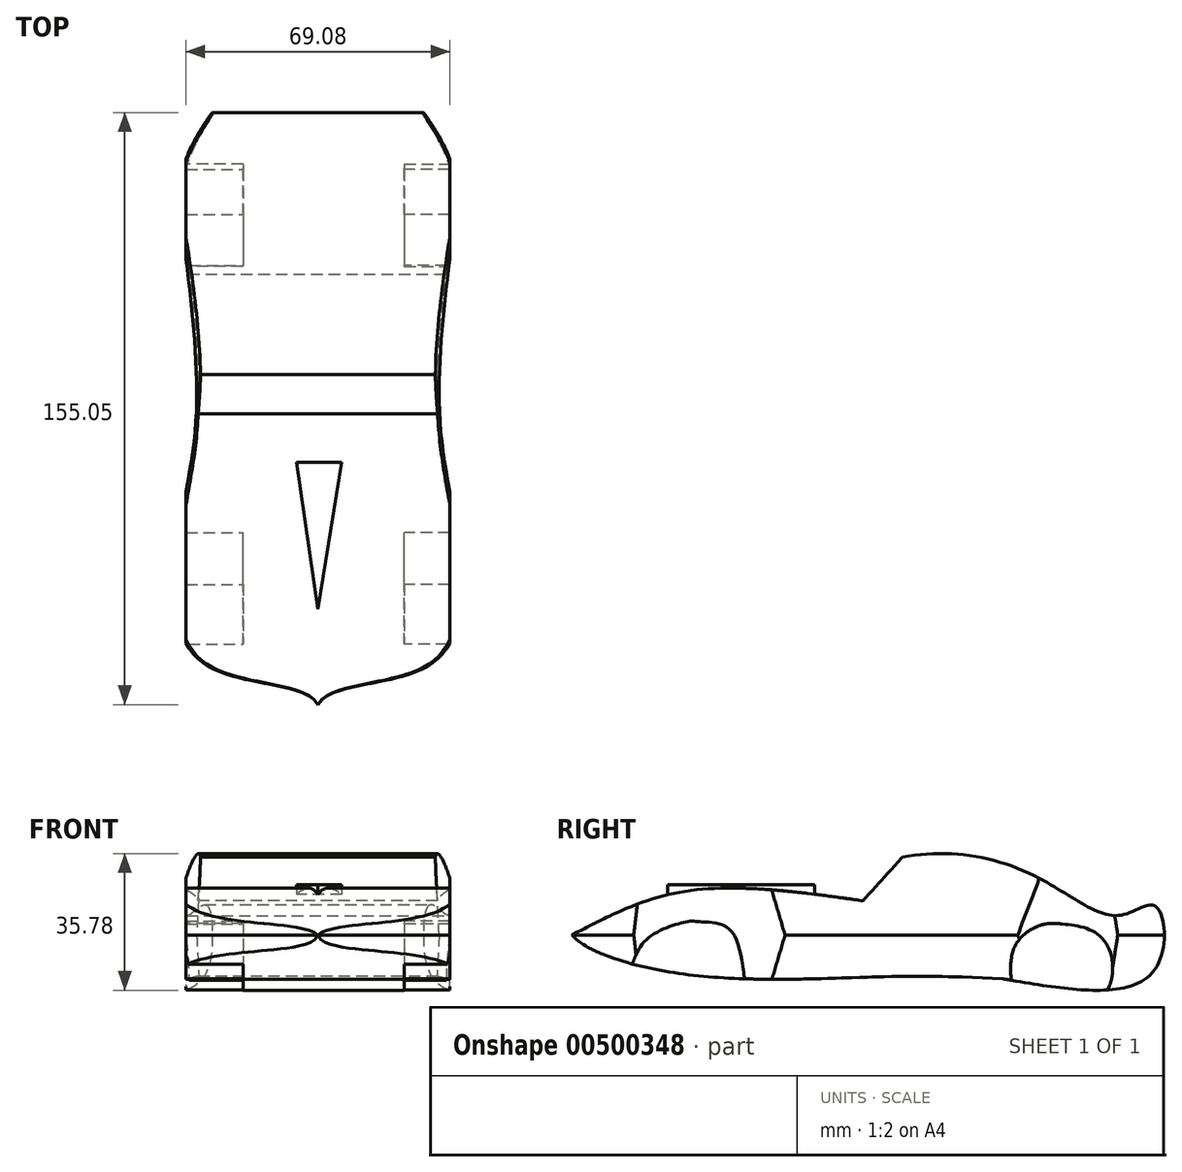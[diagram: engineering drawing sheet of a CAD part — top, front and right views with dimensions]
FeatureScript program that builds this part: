
annotation { "Feature Type Name" : "Feature", "Feature Type Description" : "" }
export const myFeature = defineFeature(function(context is Context, id is Id, definition is map)
    precondition{}
    {
        {
            var Q0;
            Q0=qCreatedBy(makeId("Right.planeOp"),FACE);
            var sketch = newSketch(context, id + "F0", { "sketchPlane" : qUnion([Q0])});
            skFitSpline(sketch, "E0", {"points": [v(-76.2, 0) * mm, v(-46.8, 11.43) * mm, v(0, 8.98) * mm], "startDerivative": vector(60.72, 32.08) * mm, "endDerivative": vector(90.7, -12.65) * mm});
            skLineSegment(sketch, "E1", {"start": v(0, 8.98) * mm, "end": v(10.28, 20.41) * mm});
            skFitSpline(sketch, "E2", {"points": [v(10.28, 20.41) * mm, v(45.93, 14.97) * mm, v(67.22, 5.17) * mm, v(76.47, 7.62) * mm, v(76.2, -9.25) * mm, v(36.47, -11.43) * mm], "startDerivative": vector(161.08, 29.29) * mm, "endDerivative": vector(-195.53, 33.8) * mm});
            skFitSpline(sketch, "E3", {"points": [v(-76.2, 0) * mm, v(-46, -10.34) * mm, v(7.08, -10.89) * mm, v(36.47, -11.43) * mm], "startDerivative": vector(40.14, -46.2) * mm, "endDerivative": vector(78.37, -3.94) * mm});
            skSolve(sketch);
        }
        {
            var Q0;
            Q0=makeQuery(id+"F0.imprint","IMPRINT",FACE,{"disambiguationData":[TD([[makeQuery(id+"F0.imprint","IMPRINT",EDGE,{"derivedFrom":sQuery(id+"F0.wireOp",EDGE,"E0")}),-1.0]])]});
            extrude(context, id + "F1", {"entities" : qUnion([Q0]), "depth" : 69.1 * mm, "symmetric" : true});
        }
        {
            var Q0;
            Q0=qCreatedBy(makeId("Top.planeOp"),FACE);
            var sketch = newSketch(context, id + "F2", { "sketchPlane" : qUnion([Q0])});
            skFitSpline(sketch, "E4", {"points": [v(-26.72, 80.15) * mm, v(-34.96, 65.46) * mm, v(-34.8, 42.38) * mm, v(-31.84, 0) * mm, v(-36.33, -30.94) * mm, v(-30.17, -65.15) * mm, v(0, -76.19) * mm], "startDerivative": vector(-42.18, -51.28) * mm, "endDerivative": vector(55.78, -106.24) * mm});
            skLineSegment(sketch, "E5", {"start": v(-26.72, 80.15) * mm, "end": v(0, 80.15) * mm});
            skLineSegment(sketch, "E6", {"start": v(0, 80.15) * mm, "end": v(0, -76.19) * mm});
            skLineSegment(sketch, "E7", {"start": v(0, -76.19) * mm, "end": v(0, -76.19) * mm});
            skLineSegment(sketch, "E8.bottom", {"start": v(-41.74, 82.16) * mm, "end": v(46.58, 82.16) * mm});
            skLineSegment(sketch, "E8.top", {"start": v(-41.74, -104.5) * mm, "end": v(46.58, -104.5) * mm});
            skLineSegment(sketch, "E8.left", {"start": v(-41.74, 82.16) * mm, "end": v(-41.74, -104.5) * mm});
            skLineSegment(sketch, "E8.right", {"start": v(46.58, 82.16) * mm, "end": v(46.58, -104.5) * mm});
            skLineSegment(sketch, "E9.MirrorCS", {"start": v(26.72, 80.15) * mm, "end": v(0, 80.15) * mm});
            skFitSpline(sketch, "E10.MirrorCS", {"points": [v(26.72, 80.15) * mm, v(34.96, 65.46) * mm, v(34.8, 42.38) * mm, v(31.84, 0) * mm, v(36.33, -30.94) * mm, v(30.17, -65.15) * mm, v(0, -76.19) * mm], "startDerivative": vector(42.18, -51.28) * mm, "endDerivative": vector(-55.78, -106.24) * mm});
            skSolve(sketch);
        }
        {
            var Q0;
            Q0=makeQuery(id+"F2.imprint","IMPRINT",FACE,{"disambiguationData":[TD([[makeQuery(id+"F2.imprint","IMPRINT",EDGE,{"derivedFrom":sQuery(id+"F2.wireOp",EDGE,"E4")}),-1.0]])]});
            extrude(context, id + "F3", {"entities" : qUnion([Q0]), "operationType" : NewBodyOperationType.REMOVE, "depth" : 147.83 * mm, "hasDraft" : true, "draftAngle" : 3 * degree, "symmetric" : true});
        }
        {
            var Q0;
            Q0=qCreatedBy(makeId("Right.planeOp"),FACE);
            var sketch = newSketch(context, id + "F4", { "sketchPlane" : qUnion([Q0])});
            skFitSpline(sketch, "E11", {"points": [v(-44.7, 3.72) * mm, v(-49.5, 2.64) * mm, v(-57.01, -1.46) * mm, v(-60.41, -7.61) * mm], "startDerivative": vector(-15.53, -2.6) * mm, "endDerivative": vector(-7.2, -19.42) * mm});
            skFitSpline(sketch, "E12", {"points": [v(-44.7, 3.72) * mm, v(-42.48, 3.47) * mm, v(-35.3, 1.78) * mm, v(-30.77, -14.9) * mm], "startDerivative": vector(10.08, -1.72) * mm, "endDerivative": vector(3.92, -42.33) * mm});
            skFitSpline(sketch, "E13", {"points": [v(52.15, 2.92) * mm, v(46.48, 2.6) * mm, v(39.68, -3.08) * mm, v(39.36, -16.52) * mm], "startDerivative": vector(-20.62, 1.71) * mm, "endDerivative": vector(4.97, -36.46) * mm});
            skFitSpline(sketch, "E14", {"points": [v(52.15, 2.92) * mm, v(58.8, 1.62) * mm, v(63.98, -2.75) * mm, v(65.1, -11.18) * mm, v(62.68, -16.52) * mm], "startDerivative": vector(27.63, -2.93) * mm, "endDerivative": vector(-13.12, -20.82) * mm});
            skLineSegment(sketch, "E15", {"start": v(-60.41, -7.61) * mm, "end": v(-30.77, -14.9) * mm});
            skLineSegment(sketch, "E16", {"start": v(62.68, -16.52) * mm, "end": v(39.36, -16.52) * mm});
            skSolve(sketch);
        }
        {
            var Q0;
            Q0 = qSketchRegion(id + "F4", true);
            extrude(context, id + "F5", {"entities" : qUnion([Q0]), "operationType" : NewBodyOperationType.REMOVE, "depth" : 42.67 * mm, "hasSecondDirection" : true, "secondDirectionOppositeDirection" : false, "secondDirectionDepth" : 22.6 * mm});
        }
        {
            var Q0;
            Q0=makeQuery(id+"F4.imprint","IMPRINT",FACE,{"disambiguationData":[TD([[makeQuery(id+"F4.imprint","IMPRINT",EDGE,{"derivedFrom":sQuery(id+"F4.wireOp",EDGE,"E11")}),1.0]])]});
            var Q1;
            Q1=makeQuery(id+"F4.imprint","IMPRINT",FACE,{"disambiguationData":[TD([[makeQuery(id+"F4.imprint","IMPRINT",EDGE,{"derivedFrom":sQuery(id+"F4.wireOp",EDGE,"E13")}),1.0]])]});
            extrude(context, id + "F6", {"entities" : qUnion([Q0, Q1]), "operationType" : NewBodyOperationType.REMOVE, "oppositeDirection" : true, "depth" : 56.4 * mm, "offsetDistance" : 25.4 * mm, "hasSecondDirection" : true, "secondDirectionOppositeDirection" : true, "secondDirectionDepth" : 19.56 * mm});
        }
        {
            var Q0;
            Q0=qCreatedBy(makeId("Top.planeOp"),FACE);
            var sketch = newSketch(context, id + "F7", { "sketchPlane" : qUnion([Q0])});
            skLineSegment(sketch, "E17", {"start": v(-5.65, -12.66) * mm, "end": v(6.25, -12.66) * mm});
            skLineSegment(sketch, "E18", {"start": v(6.25, -12.66) * mm, "end": v(0, -51.15) * mm});
            skLineSegment(sketch, "E19", {"start": v(0, -51.15) * mm, "end": v(-5.65, -12.66) * mm});
            skSolve(sketch);
        }
        {
            var Q0;
            Q0=makeQuery(id+"F7.imprint","IMPRINT",FACE,{"disambiguationData":[TD([[makeQuery(id+"F7.imprint","IMPRINT",EDGE,{"derivedFrom":sQuery(id+"F7.wireOp",EDGE,"E17")}),-1.0]])]});
            extrude(context, id + "F8", {"entities" : qUnion([Q0]), "operationType" : NewBodyOperationType.ADD, "depth" : 13.2 * mm, "offsetDistance" : 25.4 * mm});
        }
    });
